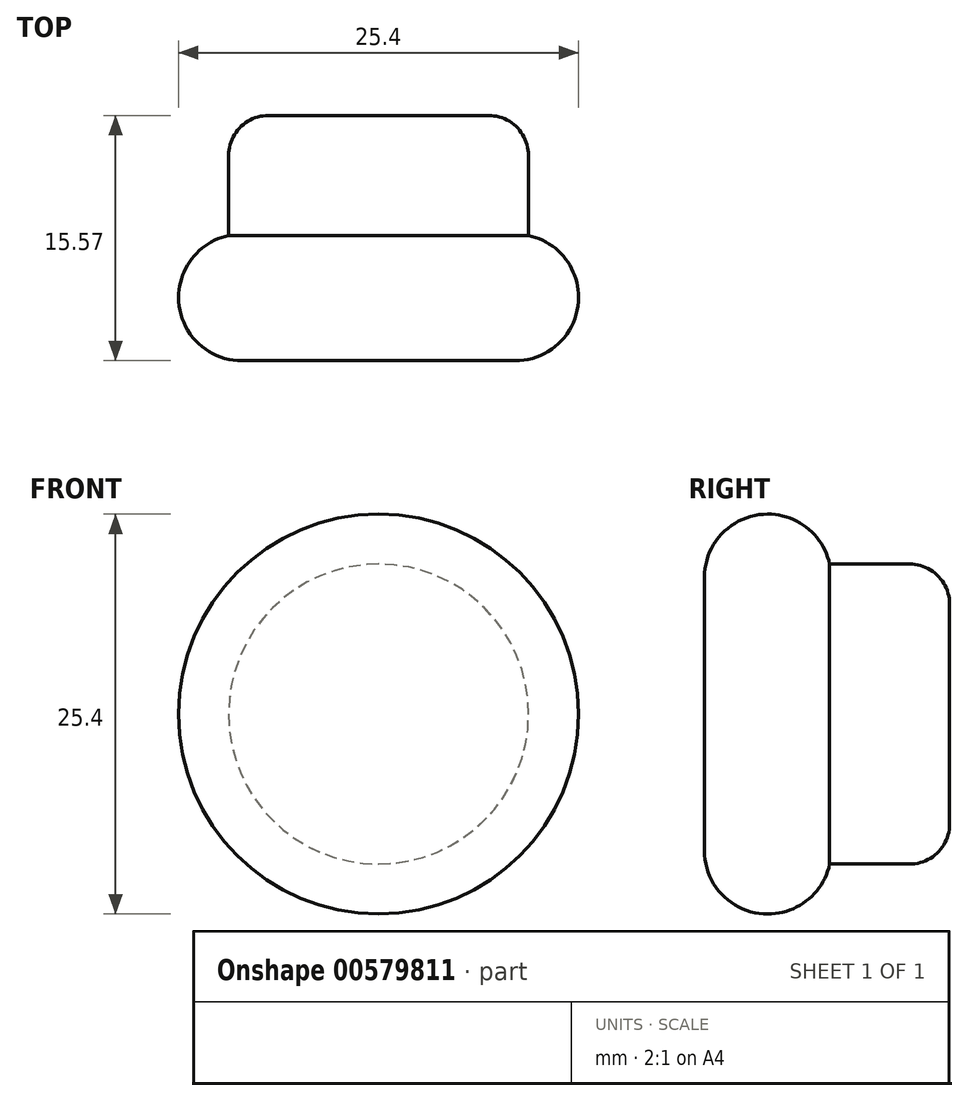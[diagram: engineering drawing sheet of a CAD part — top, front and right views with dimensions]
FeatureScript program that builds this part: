
annotation { "Feature Type Name" : "Feature", "Feature Type Description" : "" }
export const myFeature = defineFeature(function(context is Context, id is Id, definition is map)
    precondition{}
    {
        {
            var Q0;
            Q0=qCreatedBy(makeId("Front.planeOp"),FACE);
            var sketch = newSketch(context, id + "F0", { "sketchPlane" : qUnion([Q0])});
            skCircle(sketch, "E0", {"center": v(0, 0) * mm, "radius": 9.53 * mm});
            skSolve(sketch);
        }
        {
            var Q0;
            Q0=makeQuery(id+"F0.imprint","IMPRINT",FACE,{"disambiguationData":[TD([[makeQuery(id+"F0.imprint","IMPRINT",EDGE,{"derivedFrom":sQuery(id+"F0.wireOp",EDGE,"E0")}),1.0]])]});
            extrude(context, id + "F1", {"entities" : qUnion([Q0]), "depth" : 7.62 * mm, "offsetDistance" : 25.4 * mm});
        }
        {
            var Q0;
            Q0=makeQuery(id+"F1.opExtrude","CAP_FACE",FACE,{"disambiguationData":[OSD([sQuery(id+"F0.wireOp",EDGE,"E0")])],"isStart":false});
            var sketch = newSketch(context, id + "F2", { "sketchPlane" : qUnion([Q0])});
            skCircle(sketch, "E1", {"center": v(0, 0) * mm, "radius": 12.7 * mm});
            skSolve(sketch);
        }
        {
            var Q0;
            Q0=qSketchRegion(id+"F2",true);
            extrude(context, id + "F3", {"entities" : qUnion([Q0]), "operationType" : NewBodyOperationType.ADD, "depth" : 7.95 * mm, "offsetDistance" : 25.4 * mm});
        }
        {
            var Q0;
            Q0=makeQuery(id+"F3.opExtrude","CAP_EDGE",EDGE,{"disambiguationData":[OSD([sQuery(id+"F2.wireOp",EDGE,"E1")])],"isStart":false});
            var Q1;
            Q1=makeQuery(id+"F3.opExtrude","CAP_EDGE",EDGE,{"disambiguationData":[OSD([sQuery(id+"F2.wireOp",EDGE,"E1")])],"isStart":true});
            fillet(context, id + "F4", {"entities" : qUnion([Q0, Q1]), "radius" : 4 * mm, "tangentPropagation" : true, "allowEdgeOverflow" : false});
        }
        {
            var Q0;
            Q0=makeQuery(id+"F1.opExtrude","CAP_EDGE",EDGE,{"disambiguationData":[OSD([sQuery(id+"F0.wireOp",EDGE,"E0")])],"isStart":true});
            fillet(context, id + "F5", {"entities" : qUnion([Q0]), "radius" : 2.54 * mm, "tangentPropagation" : true, "allowEdgeOverflow" : false});
        }
    });
